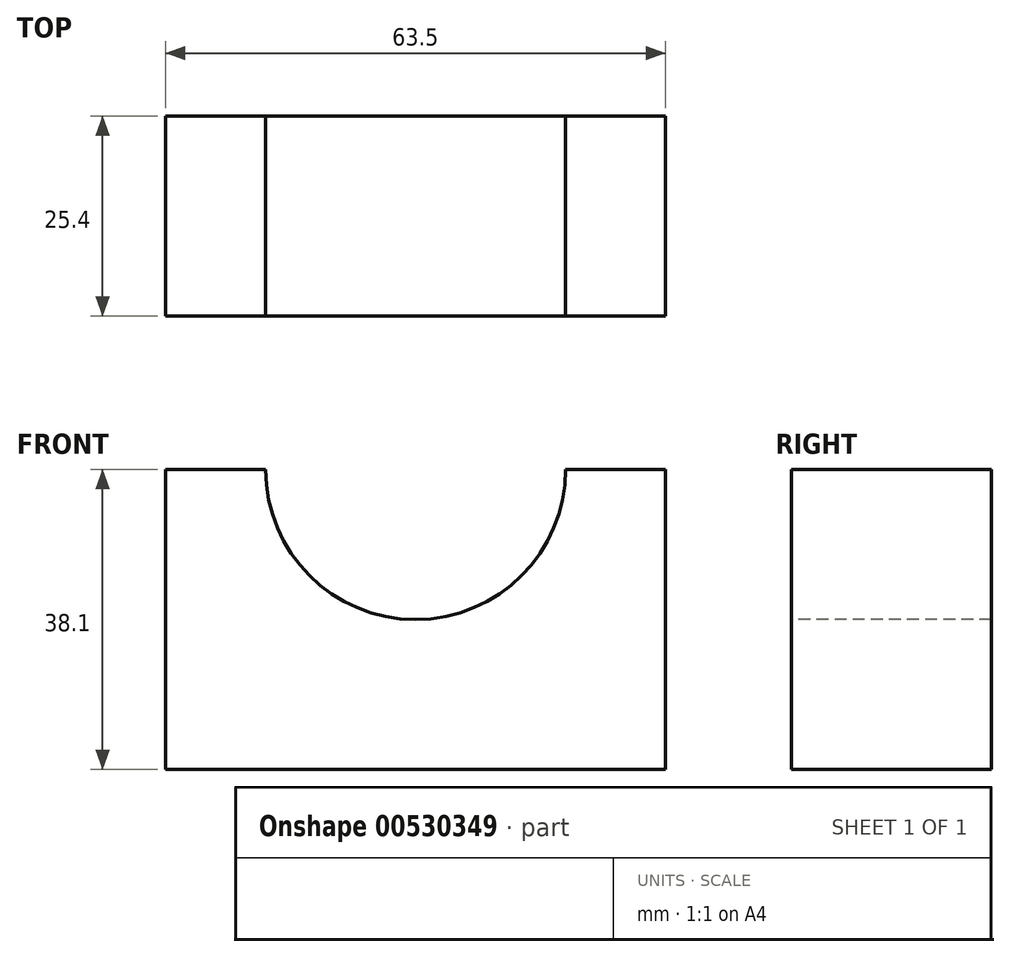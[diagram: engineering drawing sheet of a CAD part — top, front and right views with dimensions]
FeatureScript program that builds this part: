
annotation { "Feature Type Name" : "Feature", "Feature Type Description" : "" }
export const myFeature = defineFeature(function(context is Context, id is Id, definition is map)
    precondition{}
    {
        {
            var Q0;
            Q0=qCreatedBy(makeId("Front.planeOp"),FACE);
            var sketch = newSketch(context, id + "F0", { "sketchPlane" : qUnion([Q0])});
            skLineSegment(sketch, "E0", {"start": v(-76.98, 38.1) * mm, "end": v(-76.98, 0) * mm});
            skLineSegment(sketch, "E1", {"start": v(-76.98, 0) * mm, "end": v(-13.48, 0) * mm});
            skLineSegment(sketch, "E2", {"start": v(-13.48, 0) * mm, "end": v(-13.48, 38.1) * mm});
            skLineSegment(sketch, "E3", {"start": v(-13.48, 38.1) * mm, "end": v(-76.98, 38.1) * mm});
            skSolve(sketch);
        }
        {
            var Q0;
            Q0 = qSketchRegion(id + "F0", true);
            extrude(context, id + "F1", {"entities" : qUnion([Q0]), "depth" : 25.4 * mm, "offsetDistance" : 25.4 * mm});
        }
        {
            var Q0;
            Q0=makeQuery(id+"F1.opExtrude","CAP_FACE",FACE,{"disambiguationData":[OSD([sQuery(id+"F0.wireOp",EDGE,"E0"),sQuery(id+"F0.wireOp",EDGE,"E1"),sQuery(id+"F0.wireOp",EDGE,"E2"),sQuery(id+"F0.wireOp",EDGE,"E3")])],"isStart":false});
            var sketch = newSketch(context, id + "F2", { "sketchPlane" : qUnion([Q0])});
            skArc(sketch, "E4", {"start": v(-64.28, 38.1) * mm, "mid": v(-45.23, 19.05) * mm, "end": v(-26.18, 38.1) * mm});
            skSolve(sketch);
        }
        {
            var Q0;
            Q0 = qSketchRegion(id + "F2", true);
            var Q1;
            {var subQ0=sQuery(id+"F2.wireOp",EDGE,"E4");Q1=makeQuery(id+"F2.imprint","IMPRINT",FACE,{"disambiguationData":[TD([[makeQuery(id+"F2.imprint","IMPRINT",EDGE,{"derivedFrom":subQ0}),1.0]])]});}
            extrude(context, id + "F3", {"entities" : qUnion([Q0, Q1]), "operationType" : NewBodyOperationType.REMOVE, "endBound" : BoundingType.THROUGH_ALL, "oppositeDirection" : true, "depth" : 25.4 * mm, "offsetDistance" : 25.4 * mm});
        }
    });
